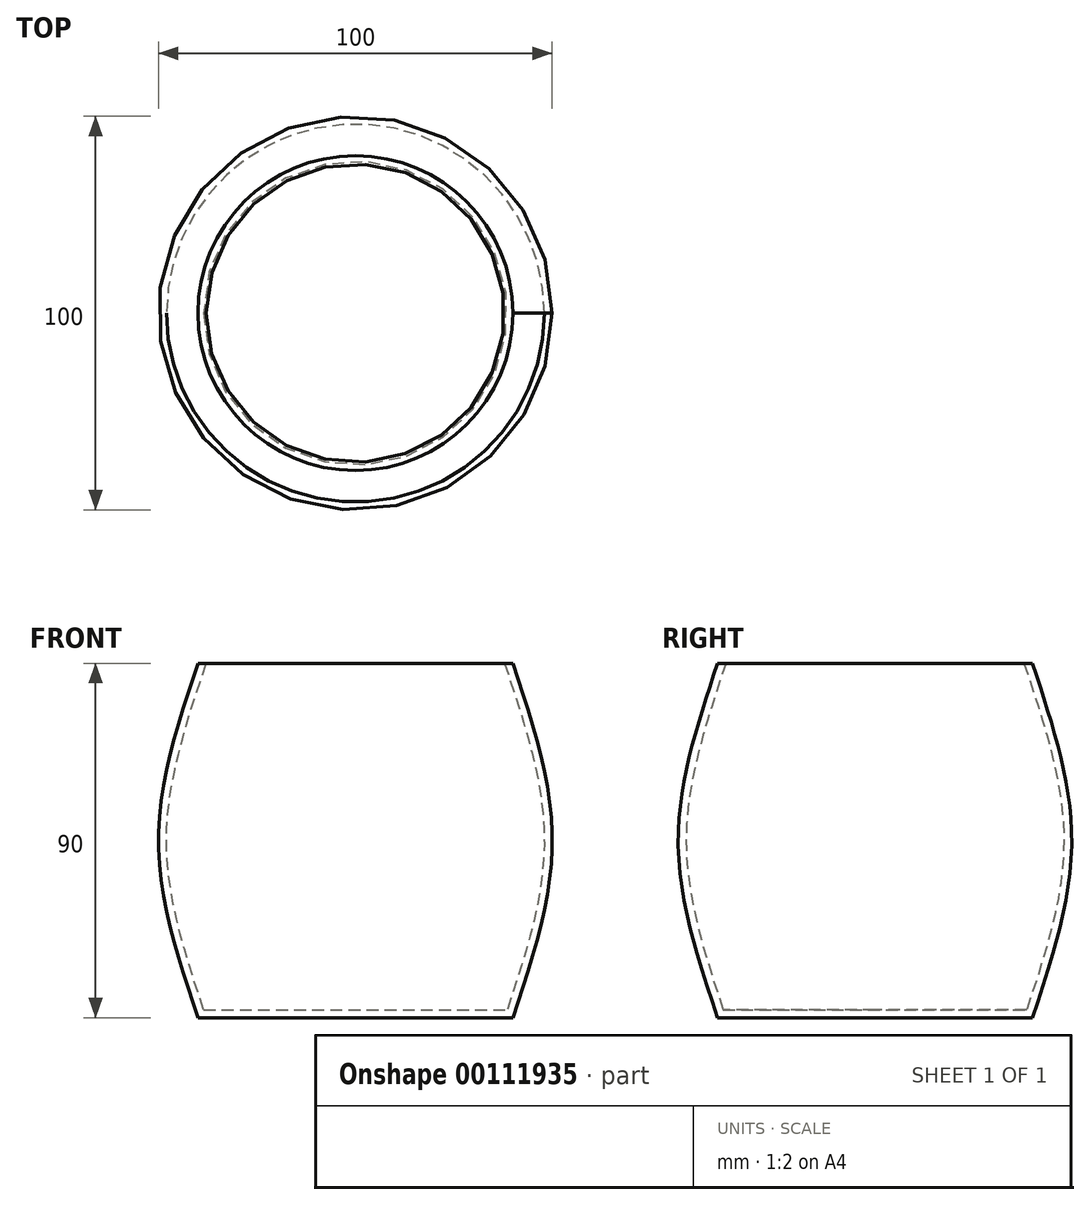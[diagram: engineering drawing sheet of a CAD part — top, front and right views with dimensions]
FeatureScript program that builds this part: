
annotation { "Feature Type Name" : "Feature", "Feature Type Description" : "" }
export const myFeature = defineFeature(function(context is Context, id is Id, definition is map)
    precondition{}
    {
        {
            var Q0;
            Q0=qCreatedBy(makeId("Top.planeOp"),FACE);
            var sketch = newSketch(context, id + "F0", { "sketchPlane" : qUnion([Q0])});
            skCircle(sketch, "E0", {"center": v(0, 0) * mm, "radius": 40 * mm});
            skSolve(sketch);
        }
        {
            var Q0;
            Q0=qCreatedBy(makeId("Top.planeOp"),FACE);
            cPlane(context, id + "F1", {"entities" : qUnion([Q0]), "cplaneType" : CPlaneType.OFFSET, "offset" : 45 * mm, "width" : 150 * mm, "height" : 150 * mm});
        }
        {
            var Q0;
            Q0=qCreatedBy(id+"F1.planeOp",FACE);
            var sketch = newSketch(context, id + "F2", { "sketchPlane" : qUnion([Q0])});
            skCircle(sketch, "E1", {"center": v(0, 0) * mm, "radius": 50 * mm});
            skSolve(sketch);
        }
        {
            var Q0;
            Q0=qCreatedBy(id+"F1.planeOp",FACE);
            cPlane(context, id + "F3", {"entities" : qUnion([Q0]), "cplaneType" : CPlaneType.OFFSET, "offset" : 45 * mm, "width" : 150 * mm, "height" : 150 * mm});
        }
        {
            var Q0;
            Q0=qCreatedBy(id+"F3.planeOp",FACE);
            var sketch = newSketch(context, id + "F4", { "sketchPlane" : qUnion([Q0])});
            skCircle(sketch, "E2", {"center": v(0, 0) * mm, "radius": 40 * mm});
            skSolve(sketch);
        }
        {
            var Q0;
            Q0=makeQuery(id+"F0.imprint","IMPRINT",FACE,{"disambiguationData":[TD([[makeQuery(id+"F0.imprint","IMPRINT",EDGE,{"derivedFrom":sQuery(id+"F0.wireOp",EDGE,"E0")}),1.0]])]});
            var Q1;
            Q1=makeQuery(id+"F2.imprint","IMPRINT",FACE,{"disambiguationData":[TD([[makeQuery(id+"F2.imprint","IMPRINT",EDGE,{"derivedFrom":sQuery(id+"F2.wireOp",EDGE,"E1")}),1.0]])]});
            var Q2;
            Q2=makeQuery(id+"F4.imprint","IMPRINT",FACE,{"disambiguationData":[TD([[makeQuery(id+"F4.imprint","IMPRINT",EDGE,{"derivedFrom":sQuery(id+"F4.wireOp",EDGE,"E2")}),1.0]])]});
            loft(context, id + "F5", {"sheetProfilesArray" : [{ "sheetProfileEntities" : qUnion([Q0]) }, { "sheetProfileEntities" : qUnion([Q1]) }, { "sheetProfileEntities" : qUnion([Q2]) }]});
        }
        {
            var Q0;
            Q0=qCreatedBy(makeId("Right.planeOp"),FACE);
            cPlane(context, id + "F6", {"entities" : qUnion([Q0]), "cplaneType" : CPlaneType.OFFSET, "offset" : 41 * mm, "oppositeDirection" : true, "width" : 150 * mm, "height" : 150 * mm});
        }
        {
            var Q0;
            Q0=makeQuery(id+"F5.opLoft","CAP_FACE",FACE,{"disambiguationData":[OSD([makeQuery(id+"F4.imprint","IMPRINT",FACE,{"disambiguationData":[TD([[makeQuery(id+"F4.imprint","IMPRINT",EDGE,{"derivedFrom":sQuery(id+"F4.wireOp",EDGE,"E2")}),1.0]])]})])],"isStart":true});
            var Q1;
            Q1=makeQuery(id+"F5.opLoft","SWEPT_BODY",BODY,{"disambiguationData":[OSD([makeQuery(id+"F0.imprint","IMPRINT",FACE,{"disambiguationData":[TD([[makeQuery(id+"F0.imprint","IMPRINT",EDGE,{"derivedFrom":sQuery(id+"F0.wireOp",EDGE,"E0")}),1.0]])]}),sQuery(id+"F2.wireOp",EDGE,"E1"),makeQuery(id+"F4.imprint","IMPRINT",FACE,{"disambiguationData":[TD([[makeQuery(id+"F4.imprint","IMPRINT",EDGE,{"derivedFrom":sQuery(id+"F4.wireOp",EDGE,"E2")}),1.0]])]})])]});
            shell(context, id + "F7", {"entities" : qUnion([Q0]), "parts" : qUnion([Q1]), "thickness" : 2 * mm});
        }
    });
